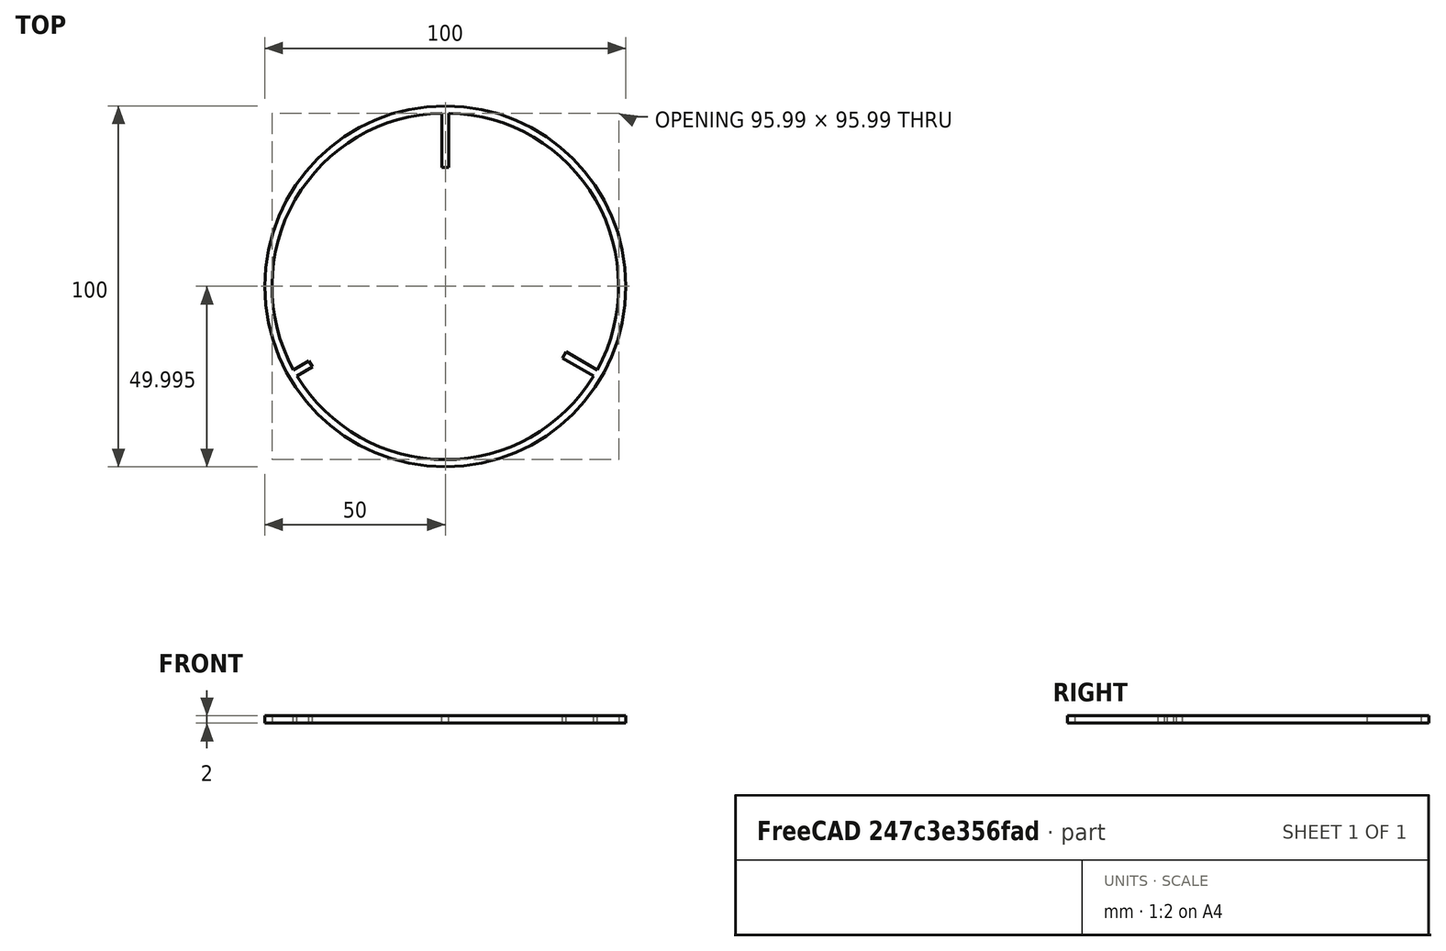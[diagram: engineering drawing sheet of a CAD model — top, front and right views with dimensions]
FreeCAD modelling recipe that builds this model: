
FCSTD DOCUMENT  (FreeCAD 0.15R4283 (Git))
Label: Dimensions_Calibration_Aid
License: CC-BY 3.0
LicenseURL: http://creativecommons.org/licenses/by/3.0/
objects: Sketcher::SketchObject×1, PartDesign::Pad×1
note: 3 computed .brp shape members not serialized (recipe doc carries the construction recipe); baked Part::Feature solids carry a one-line shape summary decoded from their .brp

FEATURE [Sketcher::SketchObject] Sketch  label="1_Base_Sketch"
  sketch-geometry (15):
    g0: Circle CenterX=0 CenterY=0 CenterZ=0 NormalX=0 NormalY=0 NormalZ=1 Radius=50
    g1: ArcOfCircle CenterX=0 CenterY=0 CenterZ=0 NormalX=0 NormalY=0 NormalZ=1 Radius=48 StartAngle=1.59163 EndAngle=3.64436
    g2: LineSegment StartX=-1 StartY=47.9896 StartZ=0 EndX=-1 EndY=32.9896 EndZ=0
    g3: LineSegment StartX=-1 StartY=32.9896 StartZ=0 EndX=1 EndY=32.9896 EndZ=0
    g4: LineSegment StartX=1 StartY=32.9896 StartZ=0 EndX=1 EndY=47.9896 EndZ=0
    g5: LineSegment [constr] StartX=0 StartY=0 StartZ=0 EndX=-43.3013 EndY=-25 EndZ=0
    g6: LineSegment [constr] StartX=0 StartY=0 StartZ=0 EndX=43.3013 EndY=-25 EndZ=0
    g7: LineSegment StartX=-42.0602 StartY=-23.1288 StartZ=0 EndX=-37.7301 EndY=-20.6288 EndZ=0
    g8: LineSegment StartX=-37.7301 StartY=-20.6288 StartZ=0 EndX=-36.7301 EndY=-22.3608 EndZ=0
    g9: LineSegment StartX=-36.7301 StartY=-22.3608 StartZ=0 EndX=-41.0602 EndY=-24.8608 EndZ=0
    g10: ArcOfCircle CenterX=0 CenterY=0 CenterZ=0 NormalX=0 NormalY=0 NormalZ=1 Radius=48 StartAngle=3.68603 EndAngle=5.73875
    g11: LineSegment StartX=41.0602 StartY=-24.8608 StartZ=0 EndX=32.3999 EndY=-19.8608 EndZ=0
    g12: LineSegment StartX=32.3999 StartY=-19.8608 StartZ=0 EndX=33.3999 EndY=-18.1288 EndZ=0
    g13: LineSegment StartX=33.3999 StartY=-18.1288 StartZ=0 EndX=42.0602 EndY=-23.1288 EndZ=0
    g14: ArcOfCircle CenterX=0 CenterY=0 CenterZ=0 NormalX=0 NormalY=0 NormalZ=1 Radius=48 StartAngle=5.78042 EndAngle=7.83315
  constraints (40):
    c: Coincident(g0,g-1)
    c: Coincident(g1,g-1)
    c: Radius(g0) = 50
    c: Radius(g1) = 48
    c: Vertical(g2)
    c: Coincident(g2,g3)
    c: Coincident(g3,g4)
    c: Vertical(g4)
    c: Symmetric(g2,g3,g-2)
    c: DistanceX(g3) = 2
    c: Coincident(g1,g2)
    c: Coincident(g14,g4)
    c: DistanceY(g4) = 15
    c: Coincident(g5,g-1)
    c: PointOnObject(g5,g0)
    c: Angle(g-2,g5) = 2.0944
    c: Coincident(g6,g-1)
    c: Symmetric(g6,g5,g-2)
    c: Coincident(g7,g8)
    c: Coincident(g8,g9)
    c: Parallel(g9,g7)
    c: Parallel(g7,g5)
    c: Symmetric(g8,g7,g5)
    c: Equal(g8,g3)
    c: Equal(g1,g10)
    c: Coincident(g1,g7)
    c: Coincident(g1,g10)
    c: Distance(g9) = 5
    c: Coincident(g9,g10)
    c: Coincident(g11,g12)
    c: Coincident(g12,g13)
    c: Parallel(g11,g13)
    c: Parallel(g13,g6)
    c: Symmetric(g11,g12,g6)
    c: Equal(g12,g3)
    c: Equal(g10,g14)
    c: Coincident(g14,g13)
    c: Coincident(g10,g14)
    c: Coincident(g10,g11)
    c: Distance(g13) = 10
FEATURE [PartDesign::Pad] Pad  label="1_Base_Pad"
  Length = 2
  Length2 = 100
  Sketch = -> Sketch
  Type = 0
